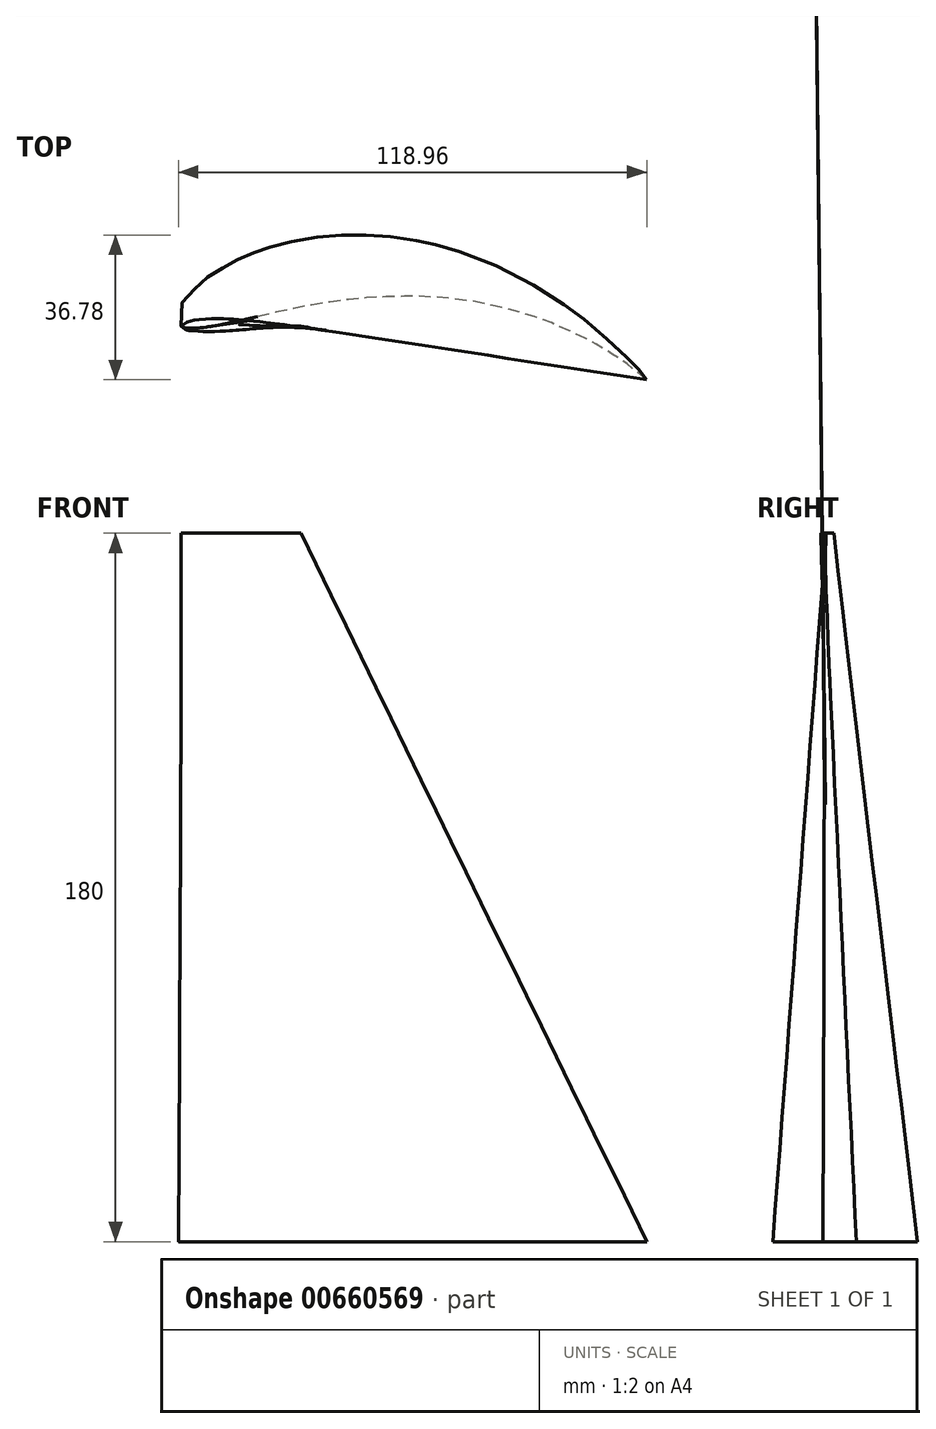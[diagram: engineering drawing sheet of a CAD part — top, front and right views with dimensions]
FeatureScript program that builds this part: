
annotation { "Feature Type Name" : "Feature", "Feature Type Description" : "" }
export const myFeature = defineFeature(function(context is Context, id is Id, definition is map)
    precondition{}
    {
        {
            var Q0;
            Q0=qCreatedBy(makeId("Top.planeOp"),FACE);
            var sketch = newSketch(context, id + "F0", { "sketchPlane" : qUnion([Q0])});
            skLineSegment(sketch, "E0", {"start": v(0.7, 6.87) * mm, "end": v(6.3, 12.24) * mm});
            skLineSegment(sketch, "E1", {"start": v(6.3, 12.24) * mm, "end": v(12.96, 16.24) * mm});
            skLineSegment(sketch, "E2", {"start": v(12.96, 16.24) * mm, "end": v(20.1, 19.3) * mm});
            skLineSegment(sketch, "E3", {"start": v(20.1, 19.3) * mm, "end": v(27.56, 21.51) * mm});
            skLineSegment(sketch, "E4", {"start": v(27.56, 21.51) * mm, "end": v(35.23, 22.74) * mm});
            skLineSegment(sketch, "E5", {"start": v(35.23, 22.74) * mm, "end": v(42.99, 23.26) * mm});
            skLineSegment(sketch, "E6", {"start": v(42.99, 23.26) * mm, "end": v(50.76, 23.04) * mm});
            skLineSegment(sketch, "E7", {"start": v(50.76, 23.04) * mm, "end": v(58.46, 22.03) * mm});
            skLineSegment(sketch, "E8", {"start": v(58.46, 22.03) * mm, "end": v(66.05, 20.35) * mm});
            skLineSegment(sketch, "E9", {"start": v(66.05, 20.35) * mm, "end": v(73.46, 18) * mm});
            skLineSegment(sketch, "E10", {"start": v(73.46, 18) * mm, "end": v(80.65, 15.05) * mm});
            skLineSegment(sketch, "E11", {"start": v(80.65, 15.05) * mm, "end": v(87.61, 11.58) * mm});
            skLineSegment(sketch, "E12", {"start": v(87.61, 11.58) * mm, "end": v(94.29, 7.6) * mm});
            skLineSegment(sketch, "E13", {"start": v(94.29, 7.6) * mm, "end": v(100.62, 3.09) * mm});
            skLineSegment(sketch, "E14", {"start": v(100.62, 3.09) * mm, "end": v(106.58, -1.86) * mm});
            skLineSegment(sketch, "E15", {"start": v(106.58, -1.86) * mm, "end": v(112.4, -7.21) * mm});
            skLineSegment(sketch, "E16", {"start": v(112.4, -7.21) * mm, "end": v(117.8, -12.72) * mm});
            skLineSegment(sketch, "E17", {"start": v(117.8, -12.72) * mm, "end": v(118.25, -13.61) * mm});
            skLineSegment(sketch, "E18", {"start": v(118.25, -13.61) * mm, "end": v(112.6, -9.15) * mm});
            skLineSegment(sketch, "E19", {"start": v(112.6, -9.15) * mm, "end": v(105.8, -4.81) * mm});
            skLineSegment(sketch, "E20", {"start": v(105.8, -4.81) * mm, "end": v(99.03, -1.22) * mm});
            skLineSegment(sketch, "E21", {"start": v(99.03, -1.22) * mm, "end": v(91.86, 1.74) * mm});
            skLineSegment(sketch, "E22", {"start": v(91.86, 1.74) * mm, "end": v(84.4, 4.08) * mm});
            skLineSegment(sketch, "E23", {"start": v(84.4, 4.08) * mm, "end": v(76.82, 5.8) * mm});
            skLineSegment(sketch, "E24", {"start": v(76.82, 5.8) * mm, "end": v(69.13, 6.96) * mm});
            skLineSegment(sketch, "E25", {"start": v(69.13, 6.96) * mm, "end": v(61.38, 7.55) * mm});
            skLineSegment(sketch, "E26", {"start": v(61.38, 7.55) * mm, "end": v(53.6, 7.6) * mm});
            skLineSegment(sketch, "E27", {"start": v(53.6, 7.6) * mm, "end": v(45.84, 7.13) * mm});
            skLineSegment(sketch, "E28", {"start": v(45.84, 7.13) * mm, "end": v(38.12, 6.22) * mm});
            skLineSegment(sketch, "E29", {"start": v(38.12, 6.22) * mm, "end": v(30.45, 4.93) * mm});
            skLineSegment(sketch, "E30", {"start": v(30.45, 4.93) * mm, "end": v(22.86, 3.28) * mm});
            skLineSegment(sketch, "E31", {"start": v(22.86, 3.28) * mm, "end": v(15.3, 1.4) * mm});
            skLineSegment(sketch, "E32", {"start": v(15.3, 1.4) * mm, "end": v(7.7, -0.18) * mm});
            skLineSegment(sketch, "E33", {"start": v(7.7, -0.18) * mm, "end": v(0, 0) * mm});
            skLineSegment(sketch, "E34", {"start": v(0, 0) * mm, "end": v(0.7, 6.87) * mm});
            skSolve(sketch);
        }
        {
            var Q0;
            Q0=makeQuery(id+"F0.imprint","IMPRINT",FACE,{"disambiguationData":[TD([[makeQuery(id+"F0.imprint","IMPRINT",EDGE,{"derivedFrom":sQuery(id+"F0.wireOp",EDGE,"E0")}),-1.0]])]});
            var sketch = newSketch(context, id + "F1", { "sketchPlane" : qUnion([Q0])});
            skPoint(sketch, "E35.0", {"position": v(0, 0) * mm});
            skPoint(sketch, "E35.1", {"position": v(0.7, 6.87) * mm});
            skPoint(sketch, "E35.2", {"position": v(6.3, 12.24) * mm});
            skPoint(sketch, "E35.3", {"position": v(7.7, -0.18) * mm});
            skPoint(sketch, "E35.4", {"position": v(15.3, 1.4) * mm});
            skPoint(sketch, "E35.5", {"position": v(22.86, 3.28) * mm});
            skPoint(sketch, "E35.6", {"position": v(12.96, 16.24) * mm});
            skPoint(sketch, "E35.7", {"position": v(20.1, 19.3) * mm});
            skPoint(sketch, "E35.8", {"position": v(50.76, 23.04) * mm});
            skPoint(sketch, "E35.9", {"position": v(73.46, 18) * mm});
            skPoint(sketch, "E35.10", {"position": v(80.65, 15.05) * mm});
            skPoint(sketch, "E35.11", {"position": v(69.13, 6.96) * mm});
            skPoint(sketch, "E35.12", {"position": v(76.82, 5.8) * mm});
            skPoint(sketch, "E35.13", {"position": v(84.4, 4.08) * mm});
            skPoint(sketch, "E35.14", {"position": v(117.8, -12.72) * mm});
            skPoint(sketch, "E35.15", {"position": v(118.25, -13.61) * mm});
            skPoint(sketch, "E35.16", {"position": v(112.6, -9.15) * mm});
            skPoint(sketch, "E35.17", {"position": v(112.4, -7.21) * mm});
            skPoint(sketch, "E35.18", {"position": v(105.8, -4.81) * mm});
            skPoint(sketch, "E35.19", {"position": v(61.38, 7.55) * mm});
            skPoint(sketch, "E35.20", {"position": v(66.05, 20.35) * mm});
            skPoint(sketch, "E35.21", {"position": v(3.5, 9.55) * mm});
            skPoint(sketch, "E35.22", {"position": v(3.85, -0.09) * mm});
            skPoint(sketch, "E35.23", {"position": v(11.5, 0.62) * mm});
            skPoint(sketch, "E35.24", {"position": v(19.08, 2.34) * mm});
            skPoint(sketch, "E35.25", {"position": v(26.65, 4.1) * mm});
            skPoint(sketch, "E35.26", {"position": v(9.63, 14.24) * mm});
            skPoint(sketch, "E35.27", {"position": v(16.53, 17.77) * mm});
            skPoint(sketch, "E35.28", {"position": v(23.83, 20.4) * mm});
            skPoint(sketch, "E35.29", {"position": v(34.28, 5.58) * mm});
            skPoint(sketch, "E35.30", {"position": v(41.98, 6.68) * mm});
            skPoint(sketch, "E35.31", {"position": v(49.72, 7.37) * mm});
            skPoint(sketch, "E35.32", {"position": v(57.49, 7.58) * mm});
            skPoint(sketch, "E35.33", {"position": v(31.4, 22.13) * mm});
            skPoint(sketch, "E35.34", {"position": v(39.1, 23) * mm});
            skPoint(sketch, "E35.35", {"position": v(46.87, 23.15) * mm});
            skPoint(sketch, "E35.36", {"position": v(54.6, 22.53) * mm});
            skPoint(sketch, "E35.37", {"position": v(62.26, 21.19) * mm});
            skPoint(sketch, "E35.38", {"position": v(90.95, 9.6) * mm});
            skPoint(sketch, "E35.39", {"position": v(97.45, 5.35) * mm});
            skPoint(sketch, "E35.40", {"position": v(103.6, 0.61) * mm});
            skPoint(sketch, "E35.41", {"position": v(109.5, -4.54) * mm});
            skPoint(sketch, "E35.42", {"position": v(115.1, -9.96) * mm});
            skPoint(sketch, "E35.43", {"position": v(115.43, -11.38) * mm});
            skPoint(sketch, "E35.44", {"position": v(102.42, -3.02) * mm});
            skPoint(sketch, "E35.45", {"position": v(95.45, 0.26) * mm});
            skPoint(sketch, "E35.46", {"position": v(88.13, 2.9) * mm});
            skFitSpline(sketch, "E36", {"points": [v(0, 0) * mm, v(0.7, 6.87) * mm, v(3.5, 9.55) * mm, v(6.3, 12.24) * mm, v(9.63, 14.24) * mm, v(12.96, 16.24) * mm, v(16.53, 17.77) * mm, v(20.1, 19.3) * mm, v(23.83, 20.4) * mm, v(31.4, 22.13) * mm, v(39.1, 23) * mm, v(46.87, 23.15) * mm, v(54.6, 22.53) * mm, v(62.26, 21.19) * mm, v(66.05, 20.35) * mm, v(80.65, 15.05) * mm, v(97.45, 5.35) * mm, v(103.6, 0.61) * mm, v(112.4, -7.21) * mm, v(115.1, -9.96) * mm, v(117.8, -12.72) * mm, v(118.25, -13.61) * mm, v(115.43, -11.38) * mm, v(112.6, -9.15) * mm, v(105.8, -4.81) * mm, v(102.42, -3.02) * mm, v(95.45, 0.26) * mm, v(88.13, 2.9) * mm, v(76.82, 5.8) * mm, v(69.13, 6.96) * mm, v(61.38, 7.55) * mm, v(57.49, 7.58) * mm, v(49.72, 7.37) * mm, v(41.98, 6.68) * mm, v(34.28, 5.58) * mm, v(26.65, 4.1) * mm, v(19.08, 2.34) * mm, v(11.5, 0.62) * mm, v(7.7, -0.18) * mm, v(0, 0) * mm]});
            skSolve(sketch);
        }
        {
            var Q0;
            Q0=qCreatedBy(makeId("Top.planeOp"),FACE);
            cPlane(context, id + "F2", {"entities" : qUnion([Q0]), "cplaneType" : CPlaneType.OFFSET, "offset" : 180 * mm, "width" : 150 * mm, "height" : 150 * mm});
        }
        {
            var Q0;
            Q0=qCreatedBy(id+"F2.planeOp",FACE);
            var sketch = newSketch(context, id + "F3", { "sketchPlane" : qUnion([Q0])});
            skLineSegment(sketch, "E37", {"start": v(0, 0) * mm, "end": v(1.33, 1.02) * mm});
            skLineSegment(sketch, "E38", {"start": v(1.33, 1.02) * mm, "end": v(2.99, 1.46) * mm});
            skLineSegment(sketch, "E39", {"start": v(2.99, 1.46) * mm, "end": v(4.69, 1.7) * mm});
            skLineSegment(sketch, "E40", {"start": v(4.69, 1.7) * mm, "end": v(6.4, 1.84) * mm});
            skLineSegment(sketch, "E41", {"start": v(6.4, 1.84) * mm, "end": v(8.11, 1.9) * mm});
            skLineSegment(sketch, "E42", {"start": v(8.11, 1.9) * mm, "end": v(9.83, 1.9) * mm});
            skLineSegment(sketch, "E43", {"start": v(9.83, 1.9) * mm, "end": v(11.55, 1.84) * mm});
            skLineSegment(sketch, "E44", {"start": v(11.55, 1.84) * mm, "end": v(13.26, 1.75) * mm});
            skLineSegment(sketch, "E45", {"start": v(13.26, 1.75) * mm, "end": v(14.98, 1.62) * mm});
            skLineSegment(sketch, "E46", {"start": v(14.98, 1.62) * mm, "end": v(16.69, 1.48) * mm});
            skLineSegment(sketch, "E47", {"start": v(16.69, 1.48) * mm, "end": v(18.4, 1.3) * mm});
            skLineSegment(sketch, "E48", {"start": v(18.4, 1.3) * mm, "end": v(20.1, 1.1) * mm});
            skLineSegment(sketch, "E49", {"start": v(20.1, 1.1) * mm, "end": v(21.8, 0.9) * mm});
            skLineSegment(sketch, "E50", {"start": v(21.8, 0.9) * mm, "end": v(23.51, 0.7) * mm});
            skLineSegment(sketch, "E51", {"start": v(23.51, 0.7) * mm, "end": v(25.22, 0.48) * mm});
            skLineSegment(sketch, "E52", {"start": v(25.22, 0.48) * mm, "end": v(26.91, 0.26) * mm});
            skLineSegment(sketch, "E53", {"start": v(26.91, 0.26) * mm, "end": v(28.67, 0.06) * mm});
            skLineSegment(sketch, "E54", {"start": v(28.67, 0.06) * mm, "end": v(30.4, -0.06) * mm});
            skLineSegment(sketch, "E55", {"start": v(30.4, -0.06) * mm, "end": v(28.75, -0.06) * mm});
            skLineSegment(sketch, "E56", {"start": v(28.75, -0.06) * mm, "end": v(27.01, -0.07) * mm});
            skLineSegment(sketch, "E57", {"start": v(27.01, -0.07) * mm, "end": v(25.3, -0.15) * mm});
            skLineSegment(sketch, "E58", {"start": v(25.3, -0.15) * mm, "end": v(23.59, -0.26) * mm});
            skLineSegment(sketch, "E59", {"start": v(23.59, -0.26) * mm, "end": v(21.87, -0.37) * mm});
            skLineSegment(sketch, "E60", {"start": v(21.87, -0.37) * mm, "end": v(20.16, -0.5) * mm});
            skLineSegment(sketch, "E61", {"start": v(20.16, -0.5) * mm, "end": v(18.45, -0.66) * mm});
            skLineSegment(sketch, "E62", {"start": v(18.45, -0.66) * mm, "end": v(16.74, -0.81) * mm});
            skLineSegment(sketch, "E63", {"start": v(16.74, -0.81) * mm, "end": v(15.03, -0.95) * mm});
            skLineSegment(sketch, "E64", {"start": v(15.03, -0.95) * mm, "end": v(13.31, -1.08) * mm});
            skLineSegment(sketch, "E65", {"start": v(13.31, -1.08) * mm, "end": v(11.6, -1.2) * mm});
            skLineSegment(sketch, "E66", {"start": v(11.6, -1.2) * mm, "end": v(9.89, -1.3) * mm});
            skLineSegment(sketch, "E67", {"start": v(9.89, -1.3) * mm, "end": v(8.17, -1.39) * mm});
            skLineSegment(sketch, "E68", {"start": v(8.17, -1.39) * mm, "end": v(6.45, -1.42) * mm});
            skLineSegment(sketch, "E69", {"start": v(6.45, -1.42) * mm, "end": v(4.74, -1.4) * mm});
            skLineSegment(sketch, "E70", {"start": v(4.74, -1.4) * mm, "end": v(3.02, -1.24) * mm});
            skLineSegment(sketch, "E71", {"start": v(3.02, -1.24) * mm, "end": v(1.34, -0.94) * mm});
            skLineSegment(sketch, "E72", {"start": v(1.34, -0.94) * mm, "end": v(0, 0) * mm});
            skSolve(sketch);
        }
        {
            var Q0;
            Q0=makeQuery(id+"F3.imprint","IMPRINT",FACE,{"disambiguationData":[TD([[makeQuery(id+"F3.imprint","IMPRINT",EDGE,{"derivedFrom":sQuery(id+"F3.wireOp",EDGE,"E37")}),-1.0]])]});
            var sketch = newSketch(context, id + "F4", { "sketchPlane" : qUnion([Q0])});
            skPoint(sketch, "E73.0", {"position": v(0, 0) * mm});
            skPoint(sketch, "E73.1", {"position": v(1.33, 1.02) * mm});
            skPoint(sketch, "E73.2", {"position": v(1.34, -0.94) * mm});
            skPoint(sketch, "E73.3", {"position": v(2.99, 1.46) * mm});
            skPoint(sketch, "E73.4", {"position": v(4.69, 1.7) * mm});
            skPoint(sketch, "E73.5", {"position": v(9.83, 1.9) * mm});
            skPoint(sketch, "E73.6", {"position": v(11.55, 1.84) * mm});
            skPoint(sketch, "E73.7", {"position": v(13.26, 1.75) * mm});
            skPoint(sketch, "E73.8", {"position": v(16.69, 1.48) * mm});
            skPoint(sketch, "E73.9", {"position": v(18.4, 1.3) * mm});
            skPoint(sketch, "E73.10", {"position": v(23.51, 0.7) * mm});
            skPoint(sketch, "E73.11", {"position": v(25.22, 0.48) * mm});
            skPoint(sketch, "E73.12", {"position": v(26.91, 0.26) * mm});
            skPoint(sketch, "E73.13", {"position": v(28.67, 0.06) * mm});
            skPoint(sketch, "E73.14", {"position": v(30.4, -0.06) * mm});
            skPoint(sketch, "E73.15", {"position": v(28.75, -0.06) * mm});
            skPoint(sketch, "E73.16", {"position": v(27.01, -0.07) * mm});
            skPoint(sketch, "E73.17", {"position": v(25.3, -0.15) * mm});
            skPoint(sketch, "E73.18", {"position": v(23.59, -0.26) * mm});
            skPoint(sketch, "E73.19", {"position": v(21.87, -0.37) * mm});
            skPoint(sketch, "E73.20", {"position": v(20.16, -0.5) * mm});
            skPoint(sketch, "E73.21", {"position": v(18.45, -0.66) * mm});
            skPoint(sketch, "E73.22", {"position": v(11.6, -1.2) * mm});
            skPoint(sketch, "E73.23", {"position": v(13.31, -1.08) * mm});
            skPoint(sketch, "E73.24", {"position": v(15.03, -0.95) * mm});
            skPoint(sketch, "E73.25", {"position": v(16.74, -0.81) * mm});
            skPoint(sketch, "E73.26", {"position": v(14.98, 1.62) * mm});
            skPoint(sketch, "E73.27", {"position": v(0.2, 0.5) * mm});
            skPoint(sketch, "E73.28", {"position": v(0.67, -0.47) * mm});
            skPoint(sketch, "E73.29", {"position": v(3.56, -1.1) * mm});
            skPoint(sketch, "E73.30", {"position": v(5.6, -1.4) * mm});
            skPoint(sketch, "E73.31", {"position": v(7.31, -1.4) * mm});
            skPoint(sketch, "E73.32", {"position": v(2.16, 1.24) * mm});
            skPoint(sketch, "E73.33", {"position": v(7.26, 1.87) * mm});
            skPoint(sketch, "E73.34", {"position": v(20.96, 1) * mm});
            skPoint(sketch, "E73.35", {"position": v(22.66, 0.8) * mm});
            skPoint(sketch, "E73.36", {"position": v(29.53, 0) * mm});
            skPoint(sketch, "E73.37", {"position": v(29.57, -0.06) * mm});
            skFitSpline(sketch, "E74", {"points": [v(0, 0) * mm, v(0.66, 0.5) * mm, v(1.33, 1.02) * mm, v(2.16, 1.24) * mm, v(2.99, 1.46) * mm, v(4.69, 1.7) * mm, v(7.26, 1.87) * mm, v(9.83, 1.9) * mm, v(11.55, 1.84) * mm, v(13.26, 1.75) * mm, v(14.98, 1.62) * mm, v(16.69, 1.48) * mm, v(18.4, 1.3) * mm, v(20.96, 1) * mm, v(22.66, 0.8) * mm, v(23.51, 0.7) * mm, v(25.22, 0.48) * mm, v(26.91, 0.26) * mm, v(28.67, 0.06) * mm, v(29.53, 0) * mm, v(30.4, -0.06) * mm, v(29.57, -0.06) * mm, v(28.75, -0.06) * mm, v(27.01, -0.07) * mm, v(25.22, -0.15) * mm, v(23.59, -0.26) * mm, v(21.87, -0.37) * mm, v(19.97, -0.5) * mm, v(18.45, -0.66) * mm, v(16.74, -0.81) * mm, v(15.03, -0.95) * mm, v(13.31, -1.08) * mm, v(11.6, -1.2) * mm, v(7.31, -1.4) * mm, v(5.6, -1.4) * mm, v(2.18, -1.1) * mm, v(1.34, -0.94) * mm, v(0.67, -0.47) * mm, v(0, 0) * mm]});
            skPoint(sketch, "E75", {"position": v(25.23, 0.53) * mm});
            skPoint(sketch, "E76", {"position": v(0.31, -0.28) * mm});
            skPoint(sketch, "E77", {"position": v(1, -0.7) * mm});
            skPoint(sketch, "E78", {"position": v(1.01, -0.7) * mm});
            skPoint(sketch, "E79", {"position": v(1.01, -0.72) * mm});
            skPoint(sketch, "E80", {"position": v(0.38, 0.35) * mm});
            skPoint(sketch, "E81", {"position": v(0.38, 0.34) * mm});
            skPoint(sketch, "E82", {"position": v(0.55, 1.36) * mm});
            skPoint(sketch, "E83", {"position": v(0.66, -0.7) * mm});
            skPoint(sketch, "E84", {"position": v(0.66, -0.71) * mm});
            skPoint(sketch, "E85", {"position": v(1, 1.84) * mm});
            skSolve(sketch);
        }
        {
            var Q0;
            Q0 = qSketchRegion(id + "F4", true);
            var Q1;
            Q1 = qSketchRegion(id + "F1", true);
            var Q2;
            Q2=sQuery(id+"F1.wireOp",EDGE,"E36");
            var Q3;
            Q3=sQuery(id+"F4.wireOp",EDGE,"E74");
            loft(context, id + "F5", {"bodyType" : ToolBodyType.SURFACE, "operationType" : NewBodyOperationType.INTERSECT, "sheetProfilesArray" : [{ "sheetProfileEntities" : qUnion([Q0]) }, { "sheetProfileEntities" : qUnion([Q1]) }], "wireProfilesArray" : [{ "wireProfileEntities" : qUnion([Q2]) }, { "wireProfileEntities" : qUnion([Q3]) }]});
        }
    });
